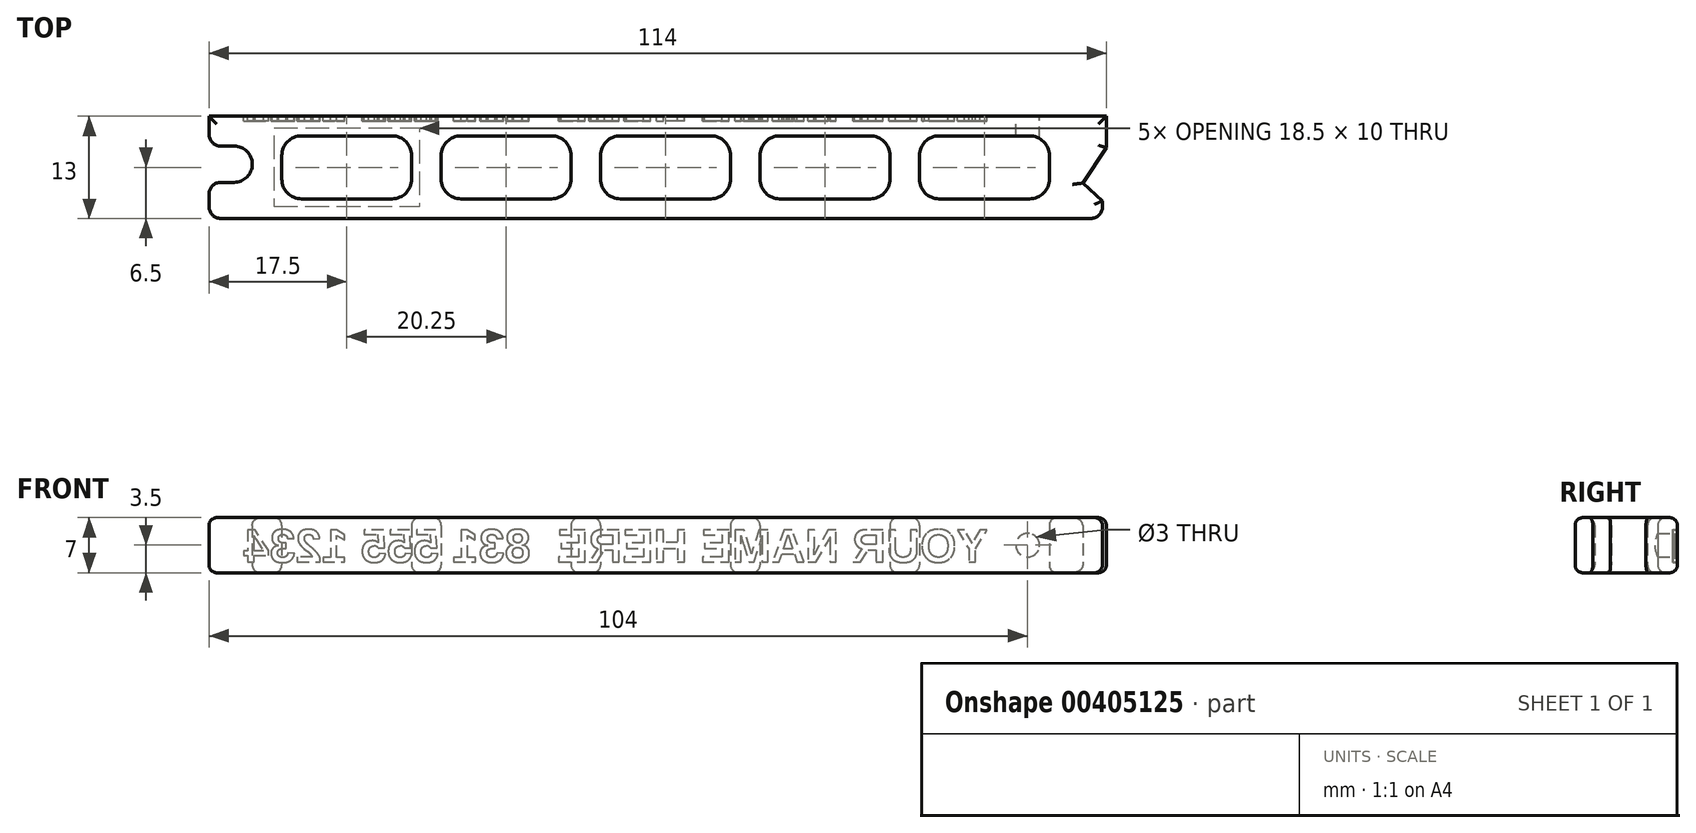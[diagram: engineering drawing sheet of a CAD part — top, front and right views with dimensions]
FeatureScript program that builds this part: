
annotation { "Feature Type Name" : "Feature", "Feature Type Description" : "" }
export const myFeature = defineFeature(function(context is Context, id is Id, definition is map)
    precondition{}
    {
        {
            var Q0;
            Q0=qCreatedBy(makeId("Top.planeOp"),FACE);
            var sketch = newSketch(context, id + "F0", { "sketchPlane" : qUnion([Q0])});
            skLineSegment(sketch, "E0.bottom", {"start": v(1.5, 0) * mm, "end": v(112, 0) * mm});
            skLineSegment(sketch, "E0.top", {"start": v(0, 13) * mm, "end": v(114, 13) * mm});
            skLineSegment(sketch, "E1", {"start": v(0, 13) * mm, "end": v(0, 10.7) * mm});
            skLineSegment(sketch, "E2.bottom", {"start": v(1.5, 4.6) * mm, "end": v(3.2, 4.6) * mm});
            skLineSegment(sketch, "E2.top", {"start": v(1.5, 9.2) * mm, "end": v(3.2, 9.2) * mm});
            skArc(sketch, "E3", {"start": v(3.2, 4.6) * mm, "mid": v(5.5, 6.9) * mm, "end": v(3.2, 9.2) * mm});
            skLineSegment(sketch, "E4.trimOffspring", {"start": v(0, 3.1) * mm, "end": v(0, 1.5) * mm});
            skLineSegment(sketch, "E5", {"start": v(0, 9.2) * mm, "end": v(0, 4.6) * mm, "construction": true});
            skLineSegment(sketch, "E6", {"start": v(0, 6.9) * mm, "end": v(3.2, 6.9) * mm, "construction": true});
            skLineSegment(sketch, "E7", {"start": v(114, 13) * mm, "end": v(114, 9) * mm});
            skPoint(sketch, "E8.visualSharp", {"position": v(0, 0) * mm});
            skArc(sketch, "E8.filletArc", {"start": v(0, 1.5) * mm, "mid": v(0.44, 0.44) * mm, "end": v(1.5, 0) * mm});
            skPoint(sketch, "E9.visualSharp", {"position": v(0, 4.6) * mm});
            skArc(sketch, "E9.filletArc", {"start": v(1.5, 4.6) * mm, "mid": v(0.44, 4.16) * mm, "end": v(0, 3.1) * mm});
            skPoint(sketch, "E10.visualSharp", {"position": v(0, 9.2) * mm});
            skArc(sketch, "E10.filletArc", {"start": v(0, 10.7) * mm, "mid": v(0.44, 9.64) * mm, "end": v(1.5, 9.2) * mm});
            skPoint(sketch, "E11.visualSharp", {"position": v(114, 4.5) * mm});
            skLineSegment(sketch, "E12", {"start": v(114, 4.5) * mm, "end": v(111, 4.5) * mm, "construction": true});
            skLineSegment(sketch, "E13", {"start": v(114, 9) * mm, "end": v(111, 4.5) * mm});
            skLineSegment(sketch, "E14", {"start": v(113.5, 2.25) * mm, "end": v(111, 4.5) * mm});
            skArc(sketch, "E15", {"start": v(112, 0) * mm, "mid": v(113.06, 0.44) * mm, "end": v(113.5, 1.5) * mm});
            skLineSegment(sketch, "E16", {"start": v(112, 1.5) * mm, "end": v(114.8, 1.5) * mm, "construction": true});
            skLineSegment(sketch, "E17", {"start": v(113.5, 2.25) * mm, "end": v(113.5, 1.5) * mm});
            skSolve(sketch);
        }
        {
            var Q0;
            Q0=makeQuery(id+"F0.imprint","IMPRINT",FACE,{"disambiguationData":[TD([[makeQuery(id+"F0.imprint","IMPRINT",EDGE,{"derivedFrom":sQuery(id+"F0.wireOp",EDGE,"E0.bottom")}),1.0]])]});
            extrude(context, id + "F1", {"entities" : qUnion([Q0]), "depth" : 7 * mm});
        }
        {
            var Q0;
            Q0=makeQuery(id+"F1.opExtrude","CAP_FACE",FACE,{"disambiguationData":[OSD([sQuery(id+"F0.wireOp",EDGE,"E0.bottom"),sQuery(id+"F0.wireOp",EDGE,"E0.top"),sQuery(id+"F0.wireOp",EDGE,"E1"),sQuery(id+"F0.wireOp",EDGE,"E2.bottom"),sQuery(id+"F0.wireOp",EDGE,"E2.top"),sQuery(id+"F0.wireOp",EDGE,"E3"),sQuery(id+"F0.wireOp",EDGE,"E4.trimOffspring"),sQuery(id+"F0.wireOp",EDGE,"E7"),sQuery(id+"F0.wireOp",EDGE,"c30ca287-96d4-4dfe-8688-3bdeec023004"),sQuery(id+"F0.wireOp",EDGE,"f645941c-dc99-4dda-a8e2-c4b280260802"),sQuery(id+"F0.wireOp",EDGE,"a89c6d0d-95b4-4aa5-8d05-a083aa38cfd4")])],"isStart":true});
            var sketch = newSketch(context, id + "F2", { "sketchPlane" : qUnion([Q0])});
            skLineSegment(sketch, "E18.bottom", {"start": v(104.25, -2.5) * mm, "end": v(92.75, -2.5) * mm});
            skLineSegment(sketch, "E18.top", {"start": v(104.25, -10.5) * mm, "end": v(92.75, -10.5) * mm});
            skLineSegment(sketch, "E18.left", {"start": v(106.75, -5) * mm, "end": v(106.75, -8) * mm});
            skLineSegment(sketch, "E18.right", {"start": v(90.25, -5) * mm, "end": v(90.25, -8) * mm});
            skLineSegment(sketch, "E19", {"start": v(106.75, -10.5) * mm, "end": v(106.75, -13) * mm, "construction": true});
            skLineSegment(sketch, "E20", {"start": v(106.75, -2.5) * mm, "end": v(106.75, 0) * mm, "construction": true});
            skPoint(sketch, "E21.visualSharp", {"position": v(90.25, -10.5) * mm});
            skArc(sketch, "E21.filletArc", {"start": v(90.25, -8) * mm, "mid": v(90.98, -9.77) * mm, "end": v(92.75, -10.5) * mm});
            skPoint(sketch, "E22.visualSharp", {"position": v(90.25, -2.5) * mm});
            skArc(sketch, "E22.filletArc", {"start": v(92.75, -2.5) * mm, "mid": v(90.98, -3.23) * mm, "end": v(90.25, -5) * mm});
            skPoint(sketch, "E23.visualSharp", {"position": v(106.75, -2.5) * mm});
            skArc(sketch, "E23.filletArc", {"start": v(106.75, -5) * mm, "mid": v(106.02, -3.23) * mm, "end": v(104.25, -2.5) * mm});
            skPoint(sketch, "E24.visualSharp", {"position": v(106.75, -10.5) * mm});
            skArc(sketch, "E24.filletArc", {"start": v(104.25, -10.5) * mm, "mid": v(106.02, -9.77) * mm, "end": v(106.75, -8) * mm});
            skLineSegment(sketch, "E25.1.0.0", {"start": v(84, -2.5) * mm, "end": v(72.5, -2.5) * mm});
            skPoint(sketch, "E25.1.0.1", {"position": v(86.5, -2.5) * mm});
            skLineSegment(sketch, "E25.1.0.2", {"start": v(84, -10.5) * mm, "end": v(72.5, -10.5) * mm});
            skPoint(sketch, "E25.1.0.3", {"position": v(86.5, -10.5) * mm});
            skLineSegment(sketch, "E25.1.0.4", {"start": v(70, -5) * mm, "end": v(70, -8) * mm});
            skLineSegment(sketch, "E25.1.0.5", {"start": v(86.5, -5) * mm, "end": v(86.5, -8) * mm});
            skPoint(sketch, "E25.1.0.6", {"position": v(70, -2.5) * mm});
            skPoint(sketch, "E25.1.0.7", {"position": v(70, -10.5) * mm});
            skArc(sketch, "E25.1.0.8", {"start": v(72.5, -2.5) * mm, "mid": v(70.73, -3.23) * mm, "end": v(70, -5) * mm});
            skArc(sketch, "E25.1.0.9", {"start": v(70, -8) * mm, "mid": v(70.73, -9.77) * mm, "end": v(72.5, -10.5) * mm});
            skArc(sketch, "E25.1.0.10", {"start": v(86.5, -5) * mm, "mid": v(85.77, -3.23) * mm, "end": v(84, -2.5) * mm});
            skArc(sketch, "E25.1.0.11", {"start": v(84, -10.5) * mm, "mid": v(85.77, -9.77) * mm, "end": v(86.5, -8) * mm});
            skLineSegment(sketch, "E25.2.0.0", {"start": v(63.75, -2.5) * mm, "end": v(52.25, -2.5) * mm});
            skPoint(sketch, "E25.2.0.1", {"position": v(66.25, -2.5) * mm});
            skLineSegment(sketch, "E25.2.0.2", {"start": v(63.75, -10.5) * mm, "end": v(52.25, -10.5) * mm});
            skPoint(sketch, "E25.2.0.3", {"position": v(66.25, -10.5) * mm});
            skLineSegment(sketch, "E25.2.0.4", {"start": v(49.75, -5) * mm, "end": v(49.75, -8) * mm});
            skLineSegment(sketch, "E25.2.0.5", {"start": v(66.25, -5) * mm, "end": v(66.25, -8) * mm});
            skPoint(sketch, "E25.2.0.6", {"position": v(49.75, -2.5) * mm});
            skPoint(sketch, "E25.2.0.7", {"position": v(49.75, -10.5) * mm});
            skArc(sketch, "E25.2.0.8", {"start": v(52.25, -2.5) * mm, "mid": v(50.48, -3.23) * mm, "end": v(49.75, -5) * mm});
            skArc(sketch, "E25.2.0.9", {"start": v(49.75, -8) * mm, "mid": v(50.48, -9.77) * mm, "end": v(52.25, -10.5) * mm});
            skArc(sketch, "E25.2.0.10", {"start": v(66.25, -5) * mm, "mid": v(65.52, -3.23) * mm, "end": v(63.75, -2.5) * mm});
            skArc(sketch, "E25.2.0.11", {"start": v(63.75, -10.5) * mm, "mid": v(65.52, -9.77) * mm, "end": v(66.25, -8) * mm});
            skLineSegment(sketch, "E25.3.0.0", {"start": v(43.5, -2.5) * mm, "end": v(32, -2.5) * mm});
            skPoint(sketch, "E25.3.0.1", {"position": v(46, -2.5) * mm});
            skLineSegment(sketch, "E25.3.0.2", {"start": v(43.5, -10.5) * mm, "end": v(32, -10.5) * mm});
            skPoint(sketch, "E25.3.0.3", {"position": v(46, -10.5) * mm});
            skLineSegment(sketch, "E25.3.0.4", {"start": v(29.5, -5) * mm, "end": v(29.5, -8) * mm});
            skLineSegment(sketch, "E25.3.0.5", {"start": v(46, -5) * mm, "end": v(46, -8) * mm});
            skPoint(sketch, "E25.3.0.6", {"position": v(29.5, -2.5) * mm});
            skPoint(sketch, "E25.3.0.7", {"position": v(29.5, -10.5) * mm});
            skArc(sketch, "E25.3.0.8", {"start": v(32, -2.5) * mm, "mid": v(30.23, -3.23) * mm, "end": v(29.5, -5) * mm});
            skArc(sketch, "E25.3.0.9", {"start": v(29.5, -8) * mm, "mid": v(30.23, -9.77) * mm, "end": v(32, -10.5) * mm});
            skArc(sketch, "E25.3.0.10", {"start": v(46, -5) * mm, "mid": v(45.27, -3.23) * mm, "end": v(43.5, -2.5) * mm});
            skArc(sketch, "E25.3.0.11", {"start": v(43.5, -10.5) * mm, "mid": v(45.27, -9.77) * mm, "end": v(46, -8) * mm});
            skLineSegment(sketch, "E25.4.0.0", {"start": v(23.25, -2.5) * mm, "end": v(11.75, -2.5) * mm});
            skPoint(sketch, "E25.4.0.1", {"position": v(25.75, -2.5) * mm});
            skLineSegment(sketch, "E25.4.0.2", {"start": v(23.25, -10.5) * mm, "end": v(11.75, -10.5) * mm});
            skPoint(sketch, "E25.4.0.3", {"position": v(25.75, -10.5) * mm});
            skLineSegment(sketch, "E25.4.0.4", {"start": v(9.25, -5) * mm, "end": v(9.25, -8) * mm});
            skLineSegment(sketch, "E25.4.0.5", {"start": v(25.75, -5) * mm, "end": v(25.75, -8) * mm});
            skPoint(sketch, "E25.4.0.6", {"position": v(9.25, -2.5) * mm});
            skPoint(sketch, "E25.4.0.7", {"position": v(9.25, -10.5) * mm});
            skArc(sketch, "E25.4.0.8", {"start": v(11.75, -2.5) * mm, "mid": v(9.98, -3.23) * mm, "end": v(9.25, -5) * mm});
            skArc(sketch, "E25.4.0.9", {"start": v(9.25, -8) * mm, "mid": v(9.98, -9.77) * mm, "end": v(11.75, -10.5) * mm});
            skArc(sketch, "E25.4.0.10", {"start": v(25.75, -5) * mm, "mid": v(25.02, -3.23) * mm, "end": v(23.25, -2.5) * mm});
            skArc(sketch, "E25.4.0.11", {"start": v(23.25, -10.5) * mm, "mid": v(25.02, -9.77) * mm, "end": v(25.75, -8) * mm});
            skLineSegment(sketch, "E25.direction1", {"start": v(92.75, -2.5) * mm, "end": v(72.5, -2.5) * mm, "construction": true});
            skSolve(sketch);
        }
        {
            var Q0;
            Q0=qSketchRegion(id+"F2",true);
            extrude(context, id + "F3", {"entities" : qUnion([Q0]), "operationType" : NewBodyOperationType.REMOVE, "endBound" : BoundingType.THROUGH_ALL, "oppositeDirection" : true, "depth" : 13.73 * mm});
        }
        {
            var Q0;
            Q0=makeQuery(id+"F1.opExtrude","CAP_FACE",FACE,{"disambiguationData":[OSD([sQuery(id+"F0.wireOp",EDGE,"E0.bottom"),sQuery(id+"F0.wireOp",EDGE,"E0.top"),sQuery(id+"F0.wireOp",EDGE,"E1"),sQuery(id+"F0.wireOp",EDGE,"E2.bottom"),sQuery(id+"F0.wireOp",EDGE,"E2.top"),sQuery(id+"F0.wireOp",EDGE,"E3"),sQuery(id+"F0.wireOp",EDGE,"E4.trimOffspring"),sQuery(id+"F0.wireOp",EDGE,"E7"),sQuery(id+"F0.wireOp",EDGE,"a89c6d0d-95b4-4aa5-8d05-a083aa38cfd4"),sQuery(id+"F0.wireOp",EDGE,"843786d9-8344-4bf4-b63c-bd20b21d23d6.filletArc"),sQuery(id+"F0.wireOp",EDGE,"E8.filletArc"),sQuery(id+"F0.wireOp",EDGE,"E9.filletArc"),sQuery(id+"F0.wireOp",EDGE,"E10.filletArc"),sQuery(id+"F0.wireOp",EDGE,"E13"),sQuery(id+"F0.wireOp",EDGE,"34148787-0765-4789-8ede-2cb2b04cca70")])],"isStart":true});
            var Q1;
            Q1=makeQuery(id+"F1.opExtrude","CAP_FACE",FACE,{"disambiguationData":[OSD([sQuery(id+"F0.wireOp",EDGE,"E0.bottom"),sQuery(id+"F0.wireOp",EDGE,"E0.top"),sQuery(id+"F0.wireOp",EDGE,"E1"),sQuery(id+"F0.wireOp",EDGE,"E2.bottom"),sQuery(id+"F0.wireOp",EDGE,"E2.top"),sQuery(id+"F0.wireOp",EDGE,"E3"),sQuery(id+"F0.wireOp",EDGE,"E4.trimOffspring"),sQuery(id+"F0.wireOp",EDGE,"E7"),sQuery(id+"F0.wireOp",EDGE,"a89c6d0d-95b4-4aa5-8d05-a083aa38cfd4"),sQuery(id+"F0.wireOp",EDGE,"843786d9-8344-4bf4-b63c-bd20b21d23d6.filletArc"),sQuery(id+"F0.wireOp",EDGE,"E8.filletArc"),sQuery(id+"F0.wireOp",EDGE,"E9.filletArc"),sQuery(id+"F0.wireOp",EDGE,"E10.filletArc"),sQuery(id+"F0.wireOp",EDGE,"E13"),sQuery(id+"F0.wireOp",EDGE,"34148787-0765-4789-8ede-2cb2b04cca70")])],"isStart":false});
            fillet(context, id + "F4", {"entities" : qUnion([Q0, Q1]), "radius" : 1 * mm, "allowEdgeOverflow" : false});
        }
        {
            var Q0;
            Q0=makeQuery(id+"F1.opExtrude","SWEPT_FACE",FACE,{"disambiguationData":[OSD([sQuery(id+"F0.wireOp",EDGE,"E0.top")])]});
            var sketch = newSketch(context, id + "F5", { "sketchPlane" : qUnion([Q0])});
            skLineSegment(sketch, "E26", {"start": v(-104, 1) * mm, "end": v(-104, 6) * mm, "construction": true});
            skCircle(sketch, "E27", {"center": v(-104, 3.5) * mm, "radius": 1.5 * mm});
            skSolve(sketch);
        }
        {
            var Q0;
            Q0=makeQuery(id+"F5.imprint","IMPRINT",FACE,{"disambiguationData":[TD([[makeQuery(id+"F5.imprint","IMPRINT",EDGE,{"derivedFrom":sQuery(id+"F5.wireOp",EDGE,"E27")}),1.0]])]});
            extrude(context, id + "F6", {"entities" : qUnion([Q0]), "operationType" : NewBodyOperationType.REMOVE, "endBound" : BoundingType.UP_TO_NEXT, "oppositeDirection" : true, "depth" : 25 * mm});
        }
        {
            var Q0;
            Q0=makeQuery(id+"F1.opExtrude","SWEPT_FACE",FACE,{"disambiguationData":[OSD([sQuery(id+"F0.wireOp",EDGE,"E0.top")])]});
            var sketch = newSketch(context, id + "F7", { "sketchPlane" : qUnion([Q0])});
            skText(sketch, "E28", { "text": "YOUR NAME HERE  831 555 1234", "fontName": "Arimo-Bold.ttf"});
            skLineSegment(sketch, "E29", {"start": v(-98.95, 5.65) * mm, "end": v(-98.95, 6) * mm, "construction": true});
            skLineSegment(sketch, "E30", {"start": v(-98.95, 1.35) * mm, "end": v(-98.95, 1) * mm, "construction": true});
            const initialGuessF7  = {"E28": [-0.09895, 0.00135, 1, 0, 0.0043]};
            skSetInitialGuess(sketch, initialGuessF7);
            skSolve(sketch);
        }
        {
            var Q0;
            Q0=qSketchRegion(id+"F7",true);
            extrude(context, id + "F8", {"entities" : qUnion([Q0]), "operationType" : NewBodyOperationType.REMOVE, "oppositeDirection" : true, "depth" : .6 * mm});
        }
    });
